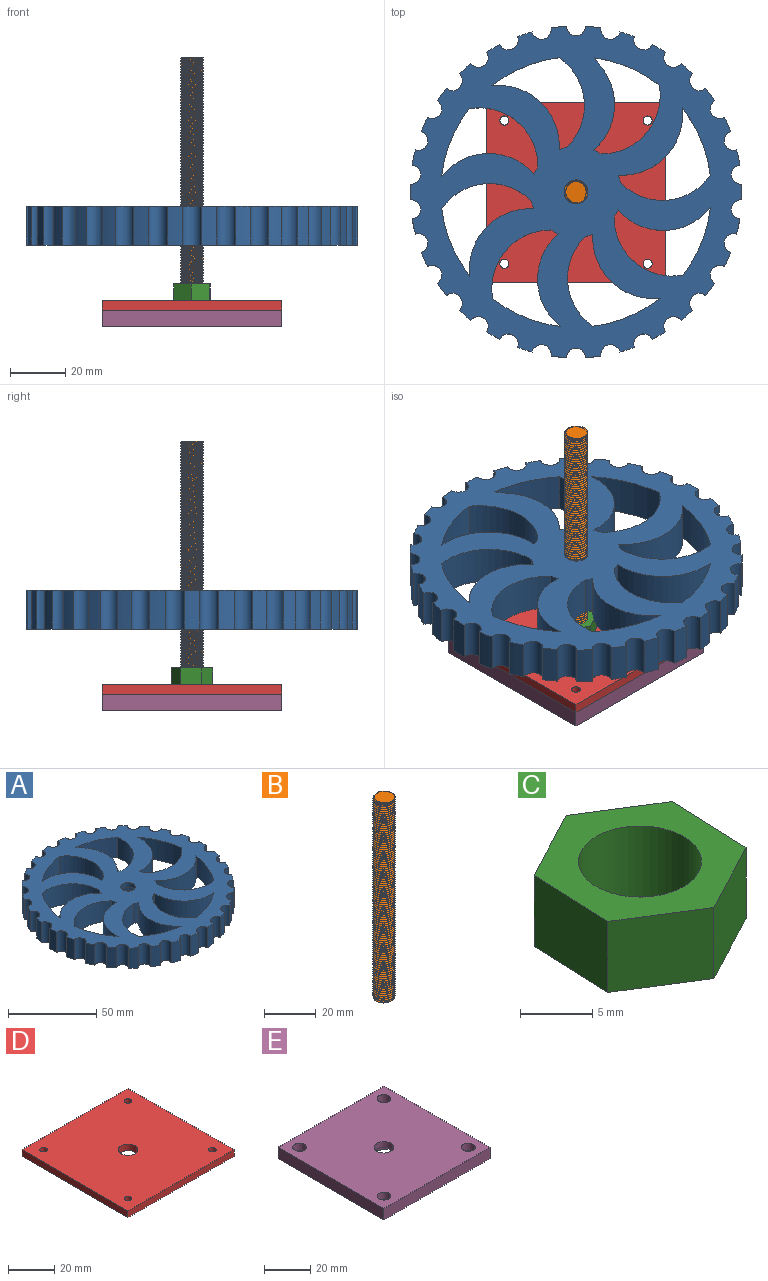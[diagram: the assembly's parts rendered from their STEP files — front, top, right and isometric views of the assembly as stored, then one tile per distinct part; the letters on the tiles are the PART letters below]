
ASSEMBLY  parts=5 mates=4
PART A: 100 faces, bbox 120x119.8x14 mm
  f0: plane 120x119.8mm, normal (0,0,1), area 6890.5mm2, adj f2,f3,f4,f5,f6,f7,f8,f9
  f1: plane 120x119.8mm, normal (0,0,-1), area 6327.6mm2, adj f2,f3,f4,f5,f6,f7,f8,f9
  f2: cylinder r=60mm len=14mm, axis (0,0,1), area 77.9mm2, adj f0,f1,f55,f66
  f3: cylinder r=60mm len=14mm, axis (0,0,1), area 77.9mm2, adj f0,f1,f64,f65
  f4: cylinder r=60mm len=14mm, axis (0,0,1), area 77.9mm2, adj f0,f1,f63,f64
  f5: cylinder r=60mm len=14mm, axis (0,0,1), area 77.9mm2, adj f0,f1,f62,f63
  f6: cylinder r=60mm len=14mm, axis (0,0,1), area 77.9mm2, adj f0,f1,f61,f62
  f7: cylinder r=60mm len=14mm, axis (0,0,1), area 77.9mm2, adj f0,f1,f60,f61
  f8: cylinder r=60mm len=14mm, axis (0,0,1), area 77.9mm2, adj f0,f1,f37,f60
  f9: cylinder r=60mm len=14mm, axis (0,0,1), area 77.9mm2, adj f0,f1,f58,f59
  f10: cylinder r=60mm len=14mm, axis (0,0,1), area 77.9mm2, adj f0,f1,f57,f58
  f11: cylinder r=60mm len=14mm, axis (0,0,1), area 77.9mm2, adj f0,f1,f56,f57
  f12: cylinder r=60mm len=14mm, axis (0,0,1), area 77.9mm2, adj f0,f1,f56,f66
  f13: cylinder r=60mm len=14mm, axis (0,0,1), area 77.9mm2, adj f0,f1,f39,f55
  f14: cylinder r=60mm len=14mm, axis (0,0,1), area 77.9mm2, adj f0,f1,f53,f54
  f15: cylinder r=60mm len=14mm, axis (0,0,1), area 77.9mm2, adj f0,f1,f52,f53
  f16: cylinder r=60mm len=14mm, axis (0,0,1), area 77.9mm2, adj f0,f1,f51,f52
  f17: cylinder r=60mm len=14mm, axis (0,0,1), area 77.9mm2, adj f0,f1,f50,f51
  f18: cylinder r=60mm len=14mm, axis (0,0,1), area 77.9mm2, adj f0,f1,f49,f50
  f19: cylinder r=60mm len=14mm, axis (0,0,1), area 77.9mm2, adj f0,f1,f48,f49
  f20: cylinder r=60mm len=14mm, axis (0,0,1), area 77.9mm2, adj f0,f1,f47,f48
  f21: cylinder r=60mm len=14mm, axis (0,0,1), area 77.9mm2, adj f0,f1,f46,f47
  f22: cylinder r=60mm len=14mm, axis (0,0,1), area 77.9mm2, adj f0,f1,f45,f46
  f23: cylinder r=60mm len=14mm, axis (0,0,1), area 77.9mm2, adj f0,f1,f44,f45
  f24: cylinder r=60mm len=14mm, axis (0,0,1), area 77.9mm2, adj f0,f1,f43,f44
  f25: cylinder r=60mm len=14mm, axis (0,0,1), area 77.9mm2, adj f0,f1,f42,f43
  f26: cylinder r=60mm len=14mm, axis (0,0,1), area 77.9mm2, adj f0,f1,f41,f42
  f27: cylinder r=60mm len=14mm, axis (0,0,1), area 77.9mm2, adj f0,f1,f41,f65
  f28: cylinder r=60mm len=14mm, axis (0,0,1), area 77.9mm2, adj f0,f1,f38,f40
  f29: cylinder r=60mm len=14mm, axis (0,0,1), area 77.9mm2, adj f0,f1,f39,f40
  f30: cylinder r=60mm len=14mm, axis (0,0,1), area 77.9mm2, adj f0,f1,f38,f54
  f31: cylinder r=60mm len=14mm, axis (0,0,1), area 77.9mm2, adj f0,f1,f37,f59
  f32: cylinder r=11.05mm len=22.1mm, axis (0,0,-1), area 499.9mm2, adj f33,f34
  f33: plane 28x28mm, normal (0,0,-1), area 232.2mm2, adj f32,f36
  f34: plane 22.1x22.1mm, normal (0,0,-1), area 330.8mm2, adj f32,f35
  f35: cylinder r=4.1mm len=8.2mm, axis (0,0,1), area 77.3mm2, adj f0,f34
  f36: cylinder r=14mm len=28mm, axis (0,0,1), area 334.3mm2, adj f1,f33
  f37: cylinder r=3.5mm len=14mm, axis (0,0,1), area 151.1mm2, adj f0,f1,f8,f31
  f38: cylinder r=3.5mm len=14mm, axis (0,0,1), area 151.1mm2, adj f0,f1,f28,f30
  f39: cylinder r=3.5mm len=14mm, axis (0,0,1), area 151.1mm2, adj f0,f1,f13,f29
  f40: cylinder r=3.5mm len=14mm, axis (0,0,1), area 151.1mm2, adj f0,f1,f28,f29
  f41: cylinder r=3.5mm len=14mm, axis (0,0,1), area 151.1mm2, adj f0,f1,f26,f27
  f42: cylinder r=3.5mm len=14mm, axis (0,0,1), area 151.1mm2, adj f0,f1,f25,f26
  f43: cylinder r=3.5mm len=14mm, axis (0,0,1), area 151.1mm2, adj f0,f1,f24,f25
  f44: cylinder r=3.5mm len=14mm, axis (0,0,1), area 151.1mm2, adj f0,f1,f23,f24
  f45: cylinder r=3.5mm len=14mm, axis (0,0,1), area 151.1mm2, adj f0,f1,f22,f23
  f46: cylinder r=3.5mm len=14mm, axis (0,0,1), area 151.1mm2, adj f0,f1,f21,f22
  f47: cylinder r=3.5mm len=14mm, axis (0,0,1), area 151.1mm2, adj f0,f1,f20,f21
  f48: cylinder r=3.5mm len=14mm, axis (0,0,1), area 151.1mm2, adj f0,f1,f19,f20
  f49: cylinder r=3.5mm len=14mm, axis (0,0,1), area 151.1mm2, adj f0,f1,f18,f19
  f50: cylinder r=3.5mm len=14mm, axis (0,0,1), area 151.1mm2, adj f0,f1,f17,f18
  f51: cylinder r=3.5mm len=14mm, axis (0,0,1), area 151.1mm2, adj f0,f1,f16,f17
  f52: cylinder r=3.5mm len=14mm, axis (0,0,1), area 151.1mm2, adj f0,f1,f15,f16
  f53: cylinder r=3.5mm len=14mm, axis (0,0,1), area 151.1mm2, adj f0,f1,f14,f15
  f54: cylinder r=3.5mm len=14mm, axis (0,0,1), area 151.1mm2, adj f0,f1,f14,f30
  f55: cylinder r=3.5mm len=14mm, axis (0,0,1), area 151.1mm2, adj f0,f1,f2,f13
  f56: cylinder r=3.5mm len=14mm, axis (0,0,1), area 151.1mm2, adj f0,f1,f11,f12
  f57: cylinder r=3.5mm len=14mm, axis (0,0,1), area 151.1mm2, adj f0,f1,f10,f11
  f58: cylinder r=3.5mm len=14mm, axis (0,0,1), area 151.1mm2, adj f0,f1,f9,f10
  f59: cylinder r=3.5mm len=14mm, axis (0,0,1), area 151.1mm2, adj f0,f1,f9,f31
  f60: cylinder r=3.5mm len=14mm, axis (0,0,1), area 151.1mm2, adj f0,f1,f7,f8
  f61: cylinder r=3.5mm len=14mm, axis (0,0,1), area 151.1mm2, adj f0,f1,f6,f7
  f62: cylinder r=3.5mm len=14mm, axis (0,0,1), area 151.1mm2, adj f0,f1,f5,f6
  f63: cylinder r=3.5mm len=14mm, axis (0,0,1), area 151.1mm2, adj f0,f1,f4,f5
  f64: cylinder r=3.5mm len=14mm, axis (0,0,1), area 151.1mm2, adj f0,f1,f3,f4
  f65: cylinder r=3.5mm len=14mm, axis (0,0,1), area 151.1mm2, adj f0,f1,f3,f27
  f66: cylinder r=3.5mm len=14mm, axis (0,0,1), area 151.1mm2, adj f0,f1,f2,f12
  f67: cylinder r=16.46mm len=14mm, axis (0,0,1), area 41mm2, adj f0,f1,f68,f70
  f68: cylinder r=21.1mm len=32.44mm, axis (0,0,1), area 520.5mm2, adj f0,f1,f67,f69
  f69: cylinder r=48.93mm len=24.36mm, axis (0,0,1), area 374.5mm2, adj f0,f1,f68,f70
  f70: cylinder r=21.8mm len=24.33mm, axis (0,0,1), area 534.7mm2, adj f0,f1,f67,f69
  f71: cylinder r=21.8mm len=24.33mm, axis (0,0,1), area 534.7mm2, adj f0,f1,f72,f74
  f72: cylinder r=16.46mm len=14mm, axis (0,0,1), area 41mm2, adj f0,f1,f71,f73
  f73: cylinder r=21.1mm len=32.44mm, axis (0,0,1), area 520.5mm2, adj f0,f1,f72,f74
  f74: cylinder r=48.93mm len=24.36mm, axis (0,0,1), area 374.5mm2, adj f0,f1,f71,f73
  f75: cylinder r=16.46mm len=14mm, axis (0,0,1), area 41mm2, adj f0,f1,f76,f78
  f76: cylinder r=21.1mm len=24.87mm, axis (0,0,1), area 520.5mm2, adj f0,f1,f75,f77
  f77: cylinder r=48.93mm len=24.45mm, axis (0,0,1), area 374.5mm2, adj f0,f1,f76,f78
  f78: cylinder r=21.8mm len=33.48mm, axis (0,0,1), area 534.7mm2, adj f0,f1,f75,f77
  f79: cylinder r=16.46mm len=14mm, axis (0,0,1), area 41mm2, adj f0,f1,f80,f82
  f80: cylinder r=21.1mm len=32.44mm, axis (0,0,1), area 520.5mm2, adj f0,f1,f79,f81
  f81: cylinder r=48.93mm len=24.36mm, axis (0,0,1), area 374.5mm2, adj f0,f1,f80,f82
  f82: cylinder r=21.8mm len=24.33mm, axis (0,0,1), area 534.7mm2, adj f0,f1,f79,f81
  f83: cylinder r=16.46mm len=14mm, axis (0,0,1), area 41mm2, adj f0,f1,f84,f86
  f84: cylinder r=21.1mm len=24.87mm, axis (0,0,1), area 520.5mm2, adj f0,f1,f83,f85
  f85: cylinder r=48.93mm len=24.45mm, axis (0,0,1), area 374.5mm2, adj f0,f1,f84,f86
  f86: cylinder r=21.8mm len=33.48mm, axis (0,0,1), area 534.7mm2, adj f0,f1,f83,f85
  f87: cylinder r=16.46mm len=14mm, axis (0,0,1), area 41mm2, adj f0,f1,f88,f90
  f88: cylinder r=21.1mm len=32.44mm, axis (0,0,1), area 520.5mm2, adj f0,f1,f87,f89
  f89: cylinder r=48.93mm len=24.36mm, axis (0,0,1), area 374.5mm2, adj f0,f1,f88,f90
  f90: cylinder r=21.8mm len=24.33mm, axis (0,0,1), area 534.7mm2, adj f0,f1,f87,f89
  f91: cylinder r=16.46mm len=14mm, axis (0,0,1), area 41mm2, adj f0,f1,f92,f95
  f92: cylinder r=21.1mm len=24.87mm, axis (0,0,1), area 520.5mm2, adj f0,f1,f91,f93
  f93: cylinder r=48.93mm len=23.33mm, axis (0,0,1), area 358.7mm2, adj f0,f1,f92,f94
  f94: cylinder r=21.1mm len=14mm, axis (0,0,1), area 52.6mm2, adj f0,f1,f93,f95
  f95: cylinder r=21.8mm len=30.28mm, axis (0,0,1), area 470.4mm2, adj f0,f1,f91,f94
  f96: cylinder r=21.1mm len=24.87mm, axis (0,0,1), area 520.5mm2, adj f0,f1,f97,f99
  f97: cylinder r=48.93mm len=24.45mm, axis (0,0,1), area 374.5mm2, adj f0,f1,f96,f98
  f98: cylinder r=21.8mm len=33.48mm, axis (0,0,1), area 534.7mm2, adj f0,f1,f97,f99
  f99: cylinder r=16.46mm len=14mm, axis (0,0,1), area 41mm2, adj f0,f1,f96,f98
PART B: 6 faces, bbox 8.8x10.1x95.6 mm
  f0: cylinder r=4.25mm len=94.4mm, axis (0,0,1), area -1334.2mm2, adj f1,f2,f4,f5
  f1: plane 8.2x8.17mm, normal (0,0,-1), area 48.8mm2, adj f0,f3,f4,f5
  f2: plane 8.2x8.16mm, normal (0,0,1), area 48.8mm2, adj f0,f3,f4,f5
  f3: bspline ~95.08x8.57mm, area 612.7mm2, adj f1,f2,f4,f5
  f4: bspline ~95.31x9.82mm, area 1484.8mm2, adj f0,f1,f2,f3
  f5: bspline ~95.15x9.82mm, area 1473.1mm2, adj f0,f1,f2,f3
PART C: 9 faces, bbox 13.3x15x6 mm
  f0: plane 6.64x6mm, normal (-0.47,0.88,0), area 45mm2, adj f1,f5,f7,f8
  f1: plane 7.5x6mm, normal (-1,0.04,0), area 45mm2, adj f0,f2,f7,f8
  f2: plane 6.35x6mm, normal (-0.53,-0.85,0), area 45mm2, adj f1,f3,f7,f8
  f3: plane 6.64x6mm, normal (0.47,-0.88,0), area 45mm2, adj f2,f4,f7,f8
  f4: plane 7.5x6mm, normal (1,-0.04,0), area 45mm2, adj f3,f5,f7,f8
  f5: plane 6.35x6mm, normal (0.53,0.85,0), area 45mm2, adj f0,f4,f7,f8
  f6: cylinder r=4.25mm len=8.5mm, axis (0,0,-1), area 160.2mm2, adj f7,f8
  f7: plane 15x13.28mm, normal (0,0,1), area 89.6mm2, adj f0,f1,f2,f3,f4,f5,f6
  f8: plane 15x13.28mm, normal (0,0,-1), area 89.6mm2, adj f0,f1,f2,f3,f4,f5,f6
PART D: 11 faces, bbox 65x65x3.5 mm
  f0: plane 65x3.5mm, normal (0,1,0), area 227.5mm2, adj f1,f8,f9,f10
  f1: plane 65x3.5mm, normal (1,0,0), area 227.5mm2, adj f0,f2,f9,f10
  f2: plane 65x3.5mm, normal (0,-1,0), area 227.5mm2, adj f1,f8,f9,f10
  f3: cylinder r=1.65mm len=3.5mm, axis (0,0,1), area 36.3mm2, adj f9,f10
  f4: cylinder r=1.65mm len=3.5mm, axis (0,0,1), area 36.3mm2, adj f9,f10
  f5: cylinder r=1.65mm len=3.5mm, axis (0,0,1), area 36.3mm2, adj f9,f10
  f6: cylinder r=1.65mm len=3.5mm, axis (0,0,1), area 36.3mm2, adj f9,f10
  f7: cylinder r=4.25mm len=8.5mm, axis (0,0,1), area 93.5mm2, adj f9,f10
  f8: plane 65x3.5mm, normal (-1,0,0), area 227.5mm2, adj f0,f2,f9,f10
  f9: plane 65x65mm, normal (0,0,-1), area 4134mm2, adj f0,f1,f2,f3,f4,f5,f6,f7
  f10: plane 65x65mm, normal (0,0,1), area 4134mm2, adj f0,f1,f2,f3,f4,f5,f6,f7
PART E: 26 faces, bbox 65x65x6 mm
  f0: plane 65x65mm, normal (0,0,-1), area 4039.9mm2, adj f2,f3,f4,f5,f15,f16,f17,f18
  f1: cylinder r=4.25mm len=8.5mm, axis (0,0,1), area 80.1mm2, adj f6,f25
  f2: plane 65x6mm, normal (0,1,0), area 390mm2, adj f0,f3,f5,f6
  f3: plane 65x6mm, normal (-1,0,0), area 390mm2, adj f0,f2,f4,f6
  f4: plane 65x6mm, normal (0,-1,0), area 390mm2, adj f0,f3,f5,f6
  f5: plane 65x6mm, normal (1,0,0), area 390mm2, adj f0,f2,f4,f6
  f6: plane 65x65mm, normal (0,0,1), area 4055.2mm2, adj f1,f2,f3,f4,f5,f7,f9,f11
  f7: cylinder r=3mm len=6mm, axis (0,0,1), area 75.4mm2, adj f6,f8
  f8: plane 6x6mm, normal (0,0,1), area 19.7mm2, adj f7,f15
  f9: cylinder r=3mm len=6mm, axis (0,0,1), area 75.4mm2, adj f6,f10
  f10: plane 6x6mm, normal (0,0,1), area 19.7mm2, adj f9,f17
  f11: cylinder r=3mm len=6mm, axis (0,0,1), area 75.4mm2, adj f6,f12
  f12: plane 6x6mm, normal (0,0,1), area 19.7mm2, adj f11,f18
  f13: cylinder r=3mm len=6mm, axis (0,0,1), area 75.4mm2, adj f6,f14
  f14: plane 6x6mm, normal (0,0,1), area 19.7mm2, adj f13,f16
  f15: cylinder r=1.65mm len=3.3mm, axis (0,0,1), area 20.7mm2, adj f0,f8
  f16: cylinder r=1.65mm len=3.3mm, axis (0,0,1), area 20.7mm2, adj f0,f14
  f17: cylinder r=1.65mm len=3.3mm, axis (0,0,1), area 20.7mm2, adj f0,f10
  f18: cylinder r=1.65mm len=3.3mm, axis (0,0,1), area 20.7mm2, adj f0,f12
  f19: plane 6.56x3.88mm, normal (-0.51,-0.86,0), area 22.9mm2, adj f0,f20,f24,f25
  f20: plane 7.62x3mm, normal (-1,0.01,0), area 22.9mm2, adj f0,f19,f21,f25
  f21: plane 6.64x3.74mm, normal (-0.49,0.87,0), area 22.9mm2, adj f0,f20,f22,f25
  f22: plane 6.56x3.88mm, normal (0.51,0.86,0), area 22.9mm2, adj f0,f21,f23,f25
  f23: plane 7.62x3mm, normal (1,-0.01,0), area 22.9mm2, adj f0,f22,f24,f25
  f24: plane 6.64x3.74mm, normal (0.49,-0.87,0), area 22.9mm2, adj f0,f19,f23,f25
  f25: plane 15.24x13.28mm, normal (0,0,-1), area 94.2mm2, adj f1,f19,f20,f21,f22,f23,f24
PLACE A t=(13.52,-42.36,-26.75)mm
PLACE B t=(13.52,-42.36,30.65)mm
PLACE C t=(13.52,-42.36,-44.55)mm
PLACE D t=(13.52,-42.36,-13.55)mm
PLACE E t=(13.52,-42.36,-48.05)mm fixed
MATE planar C.f6 <-> D.f7  axis (0,0,1) through (13.52,-42.36,-32.55)mm
MATE slider D.f7 <-> E.f1  axis (0,0,-1) through (13.52,-42.36,-42.05)mm
MATE planar A.f93 <-> D.f7  axis (0,0,-1) through (13.52,-42.36,-18.55)mm
MATE slider B.f0 <-> E.f1  axis (0,0,-1) through (13.52,-42.36,-45.05)mm
